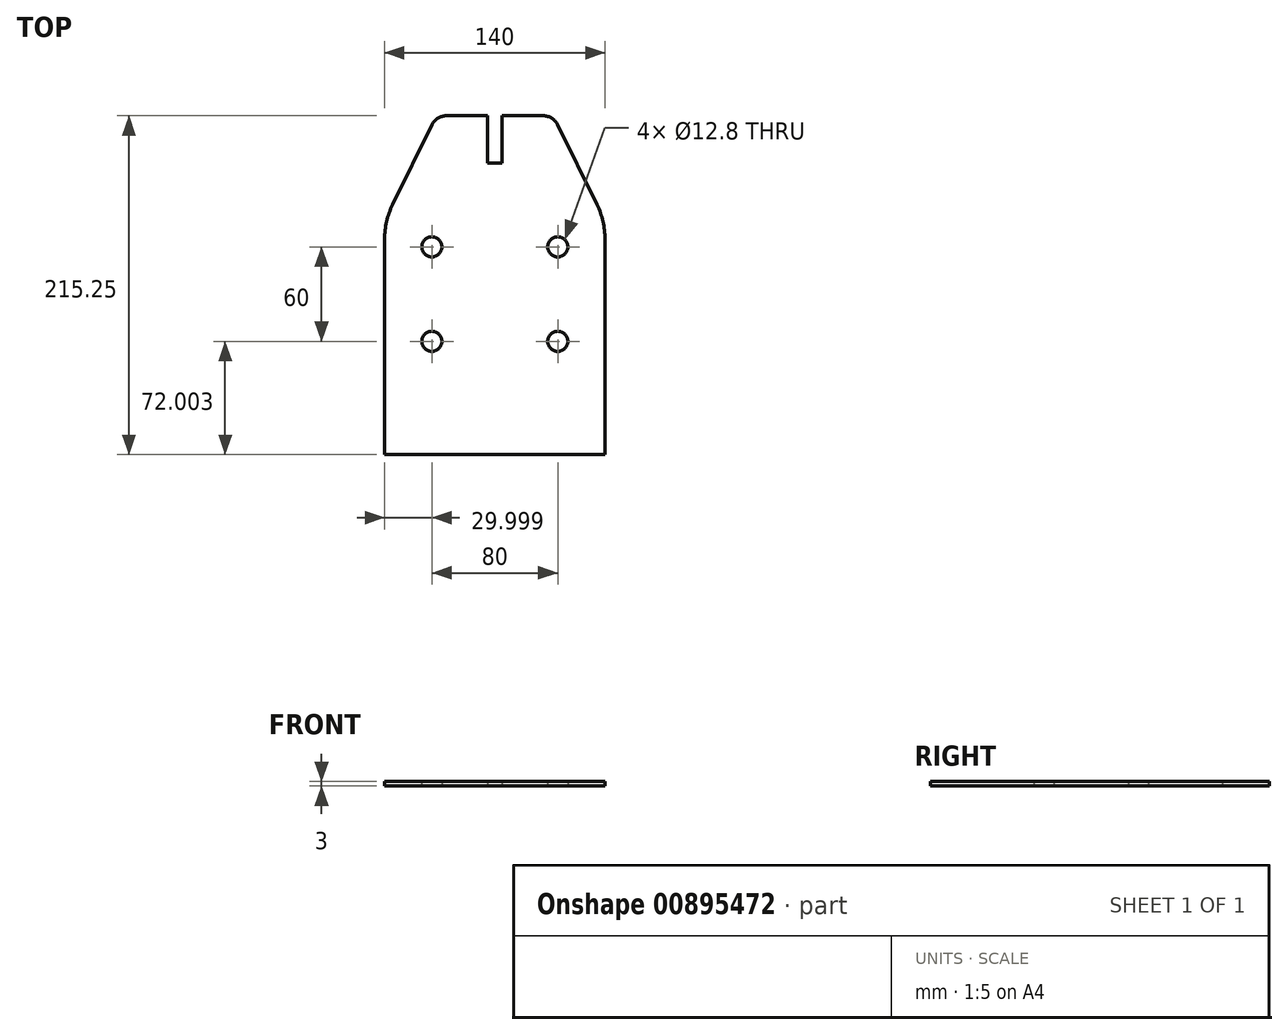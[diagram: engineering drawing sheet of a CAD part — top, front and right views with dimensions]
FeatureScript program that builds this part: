
annotation { "Feature Type Name" : "Feature", "Feature Type Description" : "" }
export const myFeature = defineFeature(function(context is Context, id is Id, definition is map)
    precondition{}
    {
        {
            var Q0;
            Q0=qCreatedBy(makeId("Top.planeOp"),FACE);
            var sketch = newSketch(context, id + "F0", { "sketchPlane" : qUnion([Q0])});
            skLineSegment(sketch, "E0", {"start": v(68.76, 318.61) * mm, "end": v(77.96, 318.61) * mm});
            skLineSegment(sketch, "E1", {"start": v(68.76, 348.61) * mm, "end": v(68.76, 318.61) * mm});
            skCircle(sketch, "E2", {"center": v(33.36, 265.36) * mm, "radius": 6.4 * mm});
            skLineSegment(sketch, "E3", {"start": v(3.36, 133.36) * mm, "end": v(3.36, 270.25) * mm});
            skLineSegment(sketch, "E4", {"start": v(68.76, 348.61) * mm, "end": v(42.52, 348.61) * mm});
            skArc(sketch, "E5", {"start": v(42.52, 348.61) * mm, "mid": v(37.21, 347.1) * mm, "end": v(33.52, 342.99) * mm});
            skLineSegment(sketch, "E6", {"start": v(143.36, 133.36) * mm, "end": v(3.36, 133.36) * mm});
            skCircle(sketch, "E7", {"center": v(113.36, 265.36) * mm, "radius": 6.4 * mm});
            skLineSegment(sketch, "E8", {"start": v(8.4, 292.11) * mm, "end": v(33.52, 342.99) * mm});
            skArc(sketch, "E9", {"start": v(8.4, 292.11) * mm, "mid": v(4.63, 281.47) * mm, "end": v(3.36, 270.25) * mm});
            skLineSegment(sketch, "E10", {"start": v(77.96, 348.61) * mm, "end": v(77.96, 318.61) * mm});
            skLineSegment(sketch, "E11", {"start": v(77.96, 348.61) * mm, "end": v(104.2, 348.61) * mm});
            skArc(sketch, "E12", {"start": v(113.2, 342.99) * mm, "mid": v(109.5, 347.1) * mm, "end": v(104.2, 348.61) * mm});
            skLineSegment(sketch, "E13", {"start": v(138.33, 292.11) * mm, "end": v(113.2, 342.99) * mm});
            skArc(sketch, "E14", {"start": v(143.36, 270.25) * mm, "mid": v(142.08, 281.47) * mm, "end": v(138.33, 292.11) * mm});
            skLineSegment(sketch, "E15", {"start": v(143.36, 133.36) * mm, "end": v(143.36, 270.25) * mm});
            skCircle(sketch, "E16", {"center": v(33.36, 205.36) * mm, "radius": 6.4 * mm});
            skCircle(sketch, "E17", {"center": v(113.36, 205.36) * mm, "radius": 6.4 * mm});
            skSolve(sketch);
        }
        {
            var Q0;
            Q0 = qSketchRegion(id + "F0", true);
            extrude(context, id + "F1", {"entities" : qUnion([Q0]), "depth" : 3 * mm, "offsetDistance" : 25 * mm});
        }
    });
